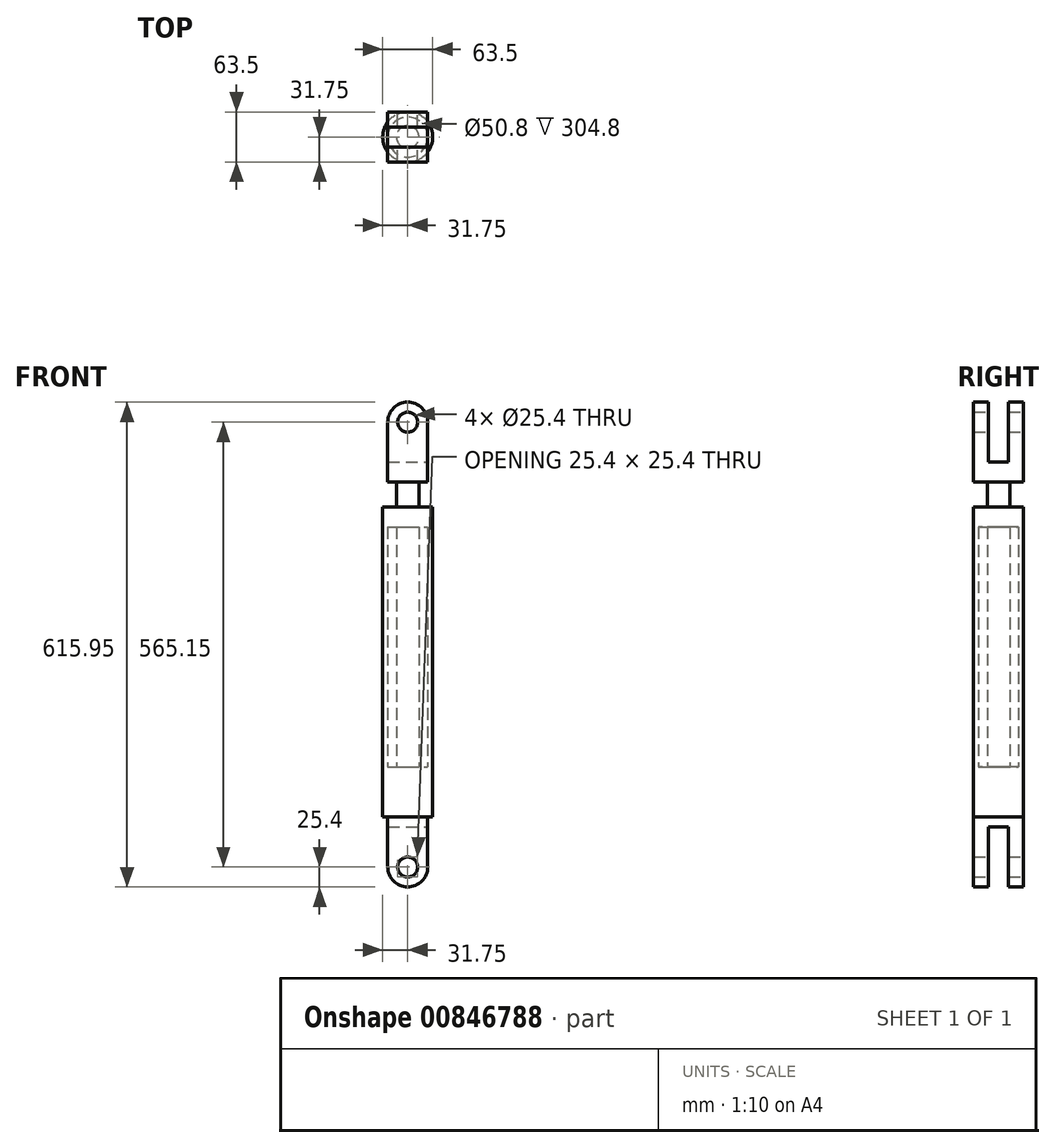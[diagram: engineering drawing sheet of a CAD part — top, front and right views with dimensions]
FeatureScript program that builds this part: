
annotation { "Feature Type Name" : "Feature", "Feature Type Description" : "" }
export const myFeature = defineFeature(function(context is Context, id is Id, definition is map)
    precondition{}
    {
        {
            var Q0;
            Q0=qCreatedBy(makeId("Front.planeOp"),FACE);
            var sketch = newSketch(context, id + "F0", { "sketchPlane" : qUnion([Q0])});
            skCircle(sketch, "E0", {"center": v(0, 0) * mm, "radius": 12.7 * mm});
            skCircle(sketch, "E1", {"center": v(0, 0) * mm, "radius": 25.4 * mm});
            skCircle(sketch, "E2", {"center": v(0, 565.15) * mm, "radius": 12.7 * mm});
            skCircle(sketch, "E3", {"center": v(0, 565.15) * mm, "radius": 25.4 * mm});
            skLineSegment(sketch, "E4", {"start": v(0, 0) * mm, "end": v(0, 565.15) * mm});
            skLineSegment(sketch, "E5", {"start": v(-14.29, 544.15) * mm, "end": v(-14.29, 127) * mm});
            skLineSegment(sketch, "E6", {"start": v(-14.29, 127) * mm, "end": v(-25.4, 127) * mm});
            skLineSegment(sketch, "E7", {"start": v(-25.4, 127) * mm, "end": v(-25.4, 88.9) * mm});
            skLineSegment(sketch, "E8", {"start": v(-25.4, 88.9) * mm, "end": v(25.4, 88.9) * mm});
            skLineSegment(sketch, "E9", {"start": v(25.4, 88.9) * mm, "end": v(25.4, 127) * mm});
            skLineSegment(sketch, "E10", {"start": v(25.4, 127) * mm, "end": v(14.29, 127) * mm});
            skLineSegment(sketch, "E11", {"start": v(14.29, 127) * mm, "end": v(14.29, 544.15) * mm});
            skLineSegment(sketch, "E12", {"start": v(-14.29, 457.2) * mm, "end": v(-31.75, 457.2) * mm});
            skLineSegment(sketch, "E13", {"start": v(-31.75, 457.2) * mm, "end": v(-31.75, 63.5) * mm});
            skLineSegment(sketch, "E14", {"start": v(-31.75, 63.5) * mm, "end": v(-25.4, 63.5) * mm});
            skLineSegment(sketch, "E15", {"start": v(-25.4, 63.5) * mm, "end": v(-25.4, 0) * mm});
            skLineSegment(sketch, "E16", {"start": v(-25.4, 127) * mm, "end": v(-25.4, 431.8) * mm});
            skLineSegment(sketch, "E17", {"start": v(-25.4, 431.8) * mm, "end": v(-14.29, 431.8) * mm});
            skLineSegment(sketch, "E18", {"start": v(-25.4, 63.5) * mm, "end": v(0, 63.5) * mm});
            skLineSegment(sketch, "E19", {"start": v(-25.4, 565.15) * mm, "end": v(-25.4, 488.95) * mm});
            skLineSegment(sketch, "E20", {"start": v(-25.4, 488.95) * mm, "end": v(0, 488.95) * mm});
            skLineSegment(sketch, "E21", {"start": v(-25.4, 508) * mm, "end": v(0, 508) * mm});
            skSolve(sketch);
        }
        {
            var Q0;
            {var subQ9=sQuery(id+"F0.wireOp",EDGE,"E6");Q0=makeQuery(id+"F0.imprint","IMPRINT",FACE,{"disambiguationData":[TD([[makeQuery(id+"F0.imprint","IMPRINT",EDGE,{"derivedFrom":subQ9}),1.0]])]});}
            var Q1;
            Q1=sQuery(id+"F0.wireOp",EDGE,"E4");
            revolve(context, id + "F1", {"surfaceOperationType" : NewSurfaceOperationType.NEW, "entities" : qUnion([Q0]), "axis" : qUnion([Q1]), "revolveType" : RevolveType.FULL});
        }
        {
            var Q0;
            {var subQ1=sQuery(id+"F0.wireOp",EDGE,"E7");Q0=makeQuery(id+"F0.imprint","IMPRINT",FACE,{"disambiguationData":[TD([[makeQuery(id+"F0.imprint","IMPRINT",EDGE,{"derivedFrom":subQ1}),-1.0]])]});}
            var Q1;
            Q1=sQuery(id+"F0.wireOp",EDGE,"E4");
            revolve(context, id + "F2", {"surfaceOperationType" : NewSurfaceOperationType.NEW, "entities" : qUnion([Q0]), "axis" : qUnion([Q1]), "revolveType" : RevolveType.FULL});
        }
        {
            var Q0;
            {var subQ0=sQuery(id+"F0.wireOp",EDGE,"E20");var subQ1=sQuery(id+"F0.wireOp",EDGE,"E4");var subQ2=makeQuery(id+"F0.imprint","INTERSECT",VERTEX,{"derivedFrom":[subQ1,subQ0]});Q0=makeQuery(id+"F0.imprint","IMPRINT",FACE,{"disambiguationData":[TD([[makeQuery(id+"F0.imprint","IMPRINT",EDGE,{"disambiguationData":[TD([[subQ2,-1.0]])],"derivedFrom":subQ1}),1.0]])]});}
            var Q1;
            {var subQ0=sQuery(id+"F0.wireOp",EDGE,"E20");var subQ1=sQuery(id+"F0.wireOp",EDGE,"E5");var subQ2=makeQuery(id+"F0.imprint","INTERSECT",VERTEX,{"derivedFrom":[subQ1,subQ0]});Q1=makeQuery(id+"F0.imprint","IMPRINT",FACE,{"disambiguationData":[TD([[makeQuery(id+"F0.imprint","IMPRINT",EDGE,{"disambiguationData":[TD([[subQ2,1.0]])],"derivedFrom":subQ1}),-1.0]])]});}
            var Q2;
            {var subQ0=sQuery(id+"F0.wireOp",EDGE,"E5");var subQ1=sQuery(id+"F0.wireOp",EDGE,"E3");var subQ2=makeQuery(id+"F0.imprint","INTERSECT",VERTEX,{"derivedFrom":[subQ1,subQ0]});Q2=makeQuery(id+"F0.imprint","IMPRINT",FACE,{"disambiguationData":[TD([[makeQuery(id+"F0.imprint","IMPRINT",EDGE,{"disambiguationData":[TD([[subQ2,-1.0]])],"derivedFrom":subQ1}),-1.0]])]});}
            var Q3;
            {var subQ0=sQuery(id+"F0.wireOp",EDGE,"E5");var subQ1=sQuery(id+"F0.wireOp",EDGE,"E3");var subQ2=makeQuery(id+"F0.imprint","INTERSECT",VERTEX,{"derivedFrom":[subQ1,subQ0]});Q3=makeQuery(id+"F0.imprint","IMPRINT",FACE,{"disambiguationData":[TD([[makeQuery(id+"F0.imprint","IMPRINT",EDGE,{"disambiguationData":[TD([[subQ2,1.0]])],"derivedFrom":subQ1}),-1.0]])]});}
            var Q4;
            Q4=makeQuery(id+"F0.imprint","IMPRINT",FACE,{"disambiguationData":[TD([[makeQuery(id+"F0.imprint","IMPRINT",EDGE,{"derivedFrom":sQuery(id+"F0.wireOp",EDGE,"E2")}),-1.0]])]});
            extrude(context, id + "F3", {"entities" : qUnion([Q0, Q1, Q2, Q3, Q4]), "operationType" : NewBodyOperationType.ADD, "endBound" : BoundingType.SYMMETRIC, "depth" : 63.5 * mm, "offsetDistance" : 25.4 * mm});
        }
        {
            var Q0;
            Q0=makeQuery(id+"F0.imprint","IMPRINT",FACE,{"disambiguationData":[TD([[makeQuery(id+"F0.imprint","IMPRINT",EDGE,{"derivedFrom":sQuery(id+"F0.wireOp",EDGE,"E0")}),-1.0]])]});
            var Q1;
            {var subQ0=sQuery(id+"F0.wireOp",EDGE,"E15");Q1=makeQuery(id+"F0.imprint","IMPRINT",FACE,{"disambiguationData":[TD([[makeQuery(id+"F0.imprint","IMPRINT",EDGE,{"derivedFrom":subQ0}),1.0]])]});}
            extrude(context, id + "F4", {"entities" : qUnion([Q0, Q1]), "operationType" : NewBodyOperationType.ADD, "endBound" : BoundingType.SYMMETRIC, "depth" : 63.5 * mm, "offsetDistance" : 25.4 * mm});
        }
        {
            var Q0;
            Q0=makeQuery(id+"F1.opRevolve","SWEPT_BODY",BODY,{"disambiguationData":[OSD([sQuery(id+"F0.wireOp",EDGE,"E4"),sQuery(id+"F0.wireOp",EDGE,"E5"),sQuery(id+"F0.wireOp",EDGE,"E6"),sQuery(id+"F0.wireOp",EDGE,"E7"),sQuery(id+"F0.wireOp",EDGE,"E8"),sQuery(id+"F0.wireOp",EDGE,"E20")])]});
            var Q1;
            Q1=qCreatedBy(makeId("Right.planeOp"),FACE);
            mirror(context, id + "F5", {"operationType" : NewBodyOperationType.ADD, "entities" : qUnion([Q0]), "mirrorPlane" : qUnion([Q1])});
        }
        {
            var Q0;
            Q0=makeQuery(id+"F2.opRevolve","SWEPT_BODY",BODY,{"disambiguationData":[OSD([sQuery(id+"F0.wireOp",EDGE,"E4"),sQuery(id+"F0.wireOp",EDGE,"E5"),sQuery(id+"F0.wireOp",EDGE,"E7"),sQuery(id+"F0.wireOp",EDGE,"E8"),sQuery(id+"F0.wireOp",EDGE,"E12"),sQuery(id+"F0.wireOp",EDGE,"E13"),sQuery(id+"F0.wireOp",EDGE,"E14"),sQuery(id+"F0.wireOp",EDGE,"E16"),sQuery(id+"F0.wireOp",EDGE,"E17"),sQuery(id+"F0.wireOp",EDGE,"E18")])]});
            var Q1;
            Q1=qCreatedBy(makeId("Right.planeOp"),FACE);
            mirror(context, id + "F6", {"operationType" : NewBodyOperationType.ADD, "entities" : qUnion([Q0]), "mirrorPlane" : qUnion([Q1])});
        }
        {
            var Q0;
            Q0=qCreatedBy(makeId("Right.planeOp"),FACE);
            var sketch = newSketch(context, id + "F7", { "sketchPlane" : qUnion([Q0])});
            skLineSegment(sketch, "E22.bottom", {"start": v(12.7, 590.55) * mm, "end": v(-12.7, 590.55) * mm});
            skLineSegment(sketch, "E22.top", {"start": v(12.7, 514.35) * mm, "end": v(-12.7, 514.35) * mm});
            skLineSegment(sketch, "E22.left", {"start": v(12.7, 590.55) * mm, "end": v(12.7, 514.35) * mm});
            skLineSegment(sketch, "E22.right", {"start": v(-12.7, 590.55) * mm, "end": v(-12.7, 514.35) * mm});
            skPoint(sketch, "E22.middle", {"position": v(0, 552.45) * mm});
            skLineSegment(sketch, "E23.bottom", {"start": v(12.7, -25.4) * mm, "end": v(-12.7, -25.4) * mm});
            skLineSegment(sketch, "E23.top", {"start": v(12.7, 50.8) * mm, "end": v(-12.7, 50.8) * mm});
            skLineSegment(sketch, "E23.left", {"start": v(12.7, -25.4) * mm, "end": v(12.7, 50.8) * mm});
            skLineSegment(sketch, "E23.right", {"start": v(-12.7, -25.4) * mm, "end": v(-12.7, 50.8) * mm});
            skPoint(sketch, "E23.middle", {"position": v(0, 12.7) * mm});
            skSolve(sketch);
        }
        {
            var Q0;
            Q0 = qSketchRegion(id + "F7", true);
            extrude(context, id + "F8", {"entities" : qUnion([Q0]), "operationType" : NewBodyOperationType.REMOVE, "endBound" : BoundingType.THROUGH_ALL, "oppositeDirection" : true, "depth" : 25.4 * mm, "offsetDistance" : 25.4 * mm, "hasSecondDirection" : true, "secondDirectionBound" : SecondDirectionBoundingType.THROUGH_ALL, "secondDirectionOppositeDirection" : false, "secondDirectionDepth" : 25.4 * mm});
        }
    });
